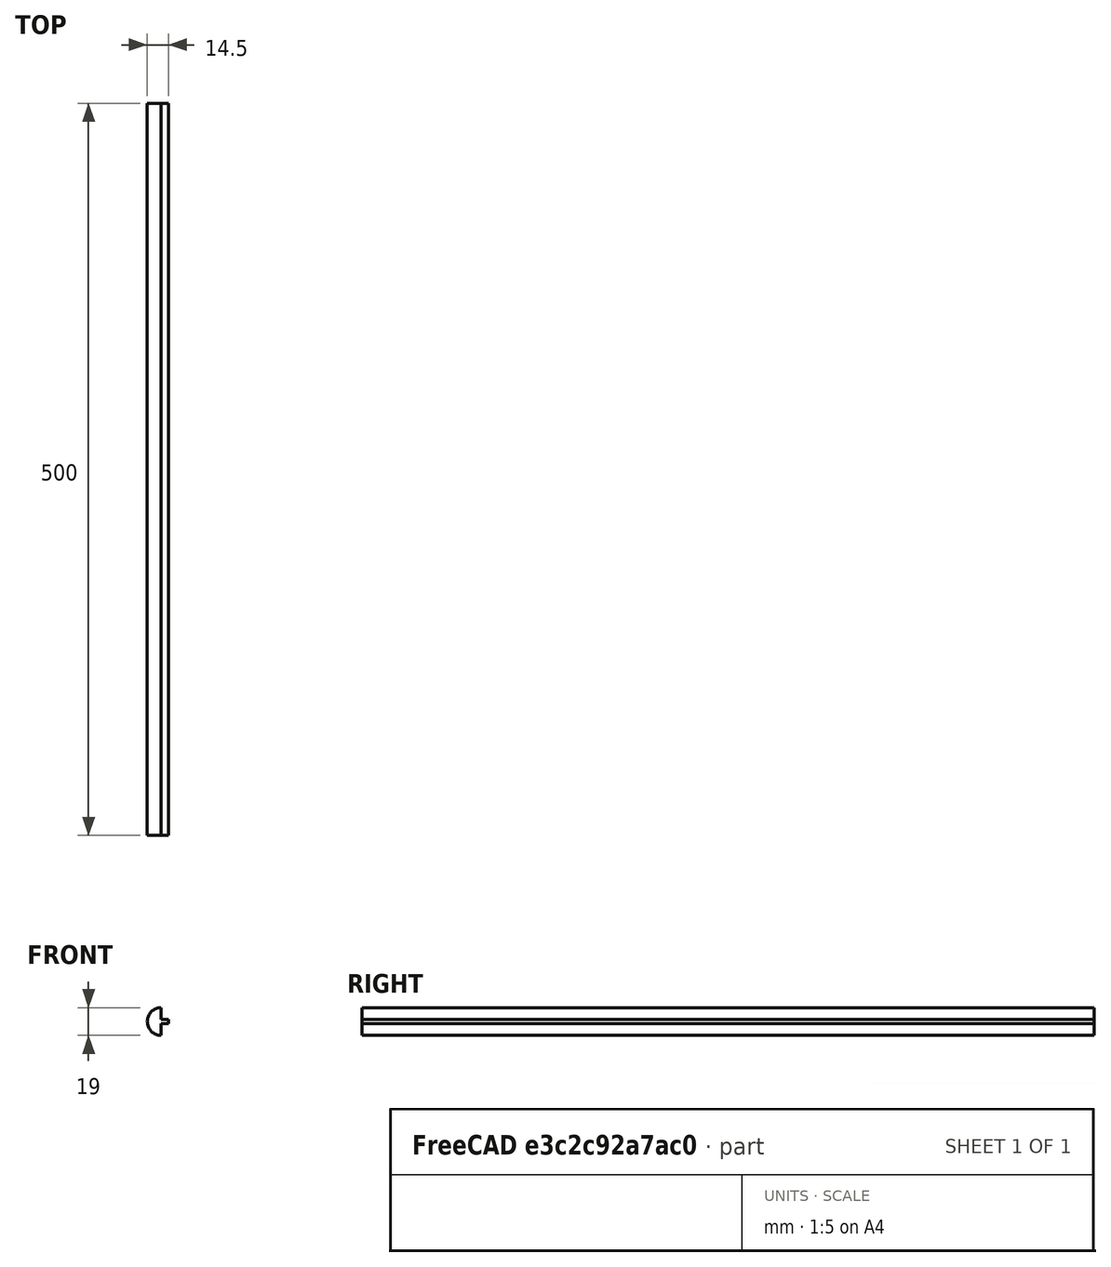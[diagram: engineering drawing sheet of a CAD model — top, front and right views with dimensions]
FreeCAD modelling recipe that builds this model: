
FCSTD DOCUMENT  (FreeCAD 0.18R14555 (Git shallow))
Label: 1001_keaboard_tmould_19_
License: All rights reserved
LicenseURL: http://en.wikipedia.org/wiki/All_rights_reserved
objects: Sketcher::SketchObject×2, Spreadsheet::Sheet×1, PartDesign::Pad×1, PartDesign::Body×1
note: 5 computed .brp shape members not serialized (recipe doc carries the construction recipe); baked Part::Feature solids carry a one-line shape summary decoded from their .brp

FEATURE [Spreadsheet::Sheet] Spreadsheet  label="xls"
  cells = B3=T-Mould; B5=Height; C5=nt; D5(nt)=19
FEATURE [Sketcher::SketchObject] Sketch002
  MapMode = 5
  Placement = pos=(0,0,0) rot=(1,0,0;1.5708rad)
  Support = -> [XZ_Plane]
  expr: Constraints[8] = xls.nt / 2
  sketch-geometry (8):
    g0: LineSegment [constr] StartX=0 StartY=0 StartZ=0 EndX=0 EndY=9.5 EndZ=0
    g1: LineSegment [constr] StartX=0 StartY=9.5 StartZ=0 EndX=0 EndY=19 EndZ=0
    g2: ArcOfCircle CenterX=0 CenterY=9.5 CenterZ=0 NormalX=0 NormalY=0 NormalZ=1 AngleXU=0 Radius=9.5 StartAngle=1.5708 EndAngle=4.71239
    g3: LineSegment StartX=0 StartY=19 StartZ=0 EndX=0 EndY=11 EndZ=0
    g4: LineSegment StartX=0 StartY=11 StartZ=0 EndX=5 EndY=11 EndZ=0
    g5: LineSegment StartX=5 StartY=11 StartZ=0 EndX=5 EndY=8 EndZ=0
    g6: LineSegment StartX=5 StartY=8 StartZ=0 EndX=0 EndY=8 EndZ=0
    g7: LineSegment StartX=0 StartY=8 StartZ=0 EndX=0 EndY=0 EndZ=0
  constraints (23):
    c: Equal(g1,g0)
    c: Vertical(g1)
    c: Vertical(g0)
    c: PointOnObject(g0,g1)
    c: Coincident(g0,g-1)
    c: Coincident(g0,g2)
    c: Coincident(g1,g2)
    c: Coincident(g2,g0)
    c: DistanceY(g0,g0) = 9.5
    c: Coincident(g7,g2)
    c: Coincident(g3,g2)
    c: Coincident(g3,g4)
    c: Equal(g3,g7)
    c: Vertical(g7)
    c: Vertical(g3)
    c: Coincident(g7,g6)
    c: Equal(g4,g6)
    c: Coincident(g5,g4)
    c: Coincident(g5,g6)
    c: Horizontal(g6)
    c: Horizontal(g4)
    c: DistanceY(g5,g5) = 3
    c: DistanceX(g4,g4) = 5
FEATURE [PartDesign::Pad] Pad
  Length = 500
  Length2 = 100
  Placement = pos=(0,0,0) rot=(1,0,0;1.5708rad)
  Profile = -> Sketch002
  Reversed = true
  Type = 0
FEATURE [Sketcher::SketchObject] Sketch
  ExternalGeometry = -> [Pad]
  MapMode = 5
  Placement = pos=(0,0,0) rot=(1,0,0;1.5708rad)
  Support = -> [XZ_Plane]
  sketch-geometry (4):
    g0: LineSegment StartX=-1.7e-15 StartY=0 StartZ=0 EndX=-1.7e-15 EndY=8.11984 EndZ=0
    g1: LineSegment StartX=-1.7e-15 StartY=8.11984 StartZ=0 EndX=8.963 EndY=9.47373 EndZ=0
    g2: LineSegment StartX=8.963 StartY=9.47373 StartZ=0 EndX=-1.8e-15 EndY=8.11984 EndZ=0
    g3: LineSegment StartX=-1.7e-15 StartY=8.11984 StartZ=0 EndX=-1.7e-15 EndY=0 EndZ=0
  constraints (9):
    c: Coincident(g2,g1)
    c: Coincident(g3,g2)
    c: Coincident(g1,g0)
    c: Coincident(g0,g3)
    c: Coincident(g0,g-3)
    c: Equal(g0,g3)
    c: Vertical(g0)
    c: Vertical(g3)
    c: Equal(g1,g2)
FEATURE [PartDesign::Body] Body
  Group = -> [Sketch002,Pad,Sketch]
  Origin = -> Origin
  Tip = -> Pad
